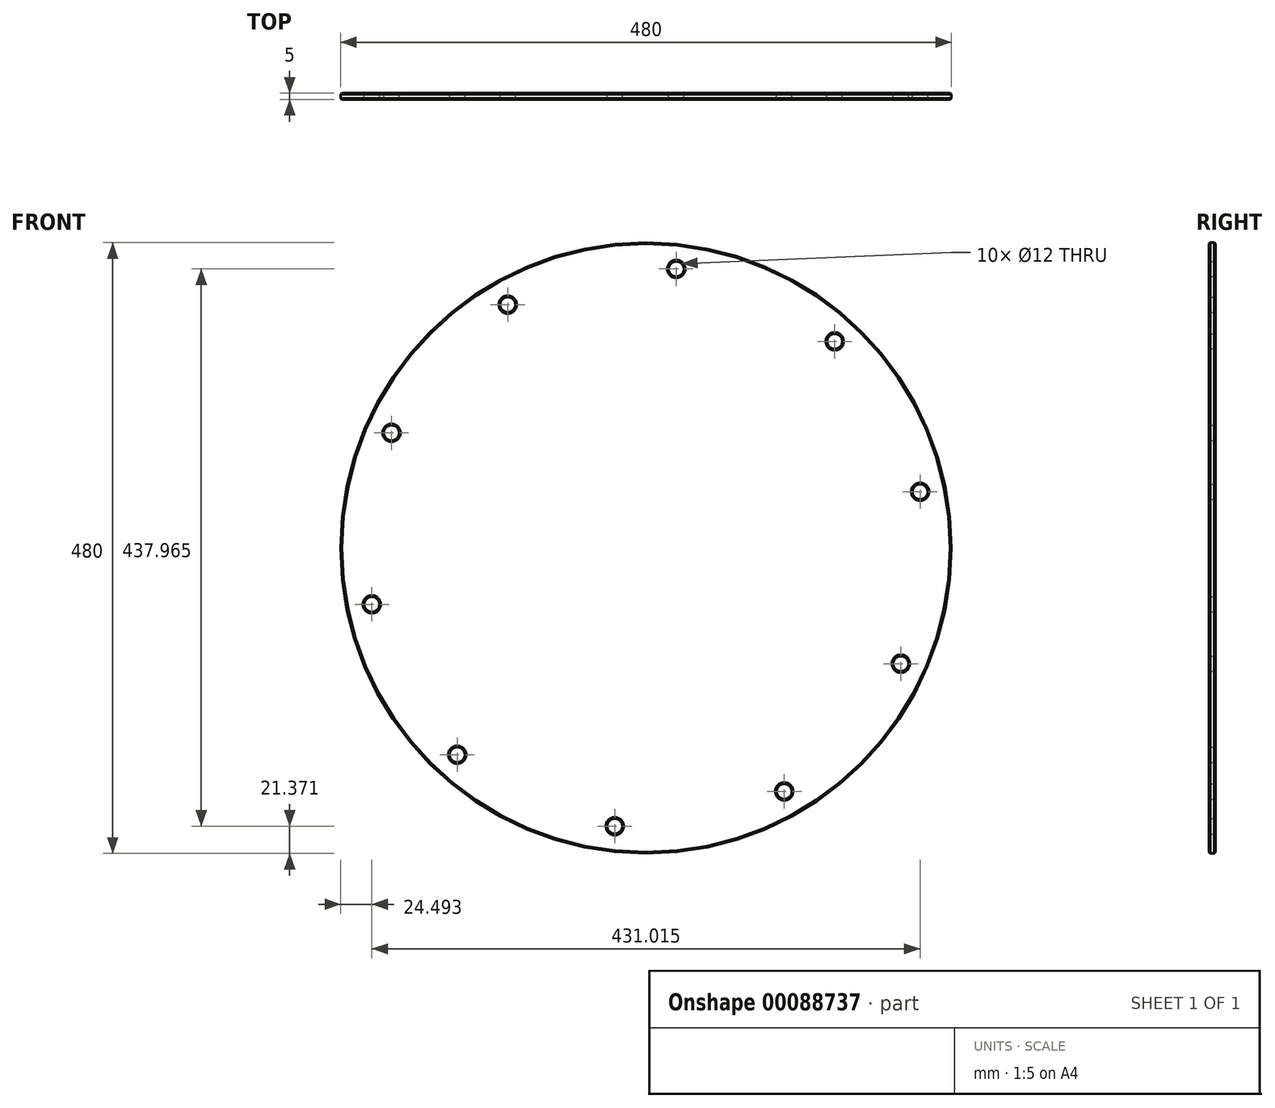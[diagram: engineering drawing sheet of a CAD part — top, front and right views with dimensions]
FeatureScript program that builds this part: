
annotation { "Feature Type Name" : "Feature", "Feature Type Description" : "" }
export const myFeature = defineFeature(function(context is Context, id is Id, definition is map)
    precondition{}
    {
        {
            var Q0;
            Q0=qCreatedBy(makeId("Front.planeOp"),FACE);
            var sketch = newSketch(context, id + "F0", { "sketchPlane" : qUnion([Q0])});
            skCircle(sketch, "E0", {"center": v(0, 0) * mm, "radius": 240 * mm});
            skCircle(sketch, "E1", {"center": v(200.35, -90.89) * mm, "radius": 6 * mm});
            skCircle(sketch, "E2", {"center": v(215.5, 44.23) * mm, "radius": 6 * mm});
            skCircle(sketch, "E3", {"center": v(148.35, 162.46) * mm, "radius": 6 * mm});
            skCircle(sketch, "E4", {"center": v(108.66, -191.3) * mm, "radius": 6 * mm});
            skCircle(sketch, "E5", {"center": v(-24.53, -218.63) * mm, "radius": 6 * mm});
            skCircle(sketch, "E6", {"center": v(-148.35, -162.46) * mm, "radius": 6 * mm});
            skCircle(sketch, "E7", {"center": v(-215.5, -44.23) * mm, "radius": 6 * mm});
            skCircle(sketch, "E8", {"center": v(-200.03, 90.54) * mm, "radius": 6 * mm});
            skCircle(sketch, "E9", {"center": v(-108.66, 191.3) * mm, "radius": 6 * mm});
            skCircle(sketch, "E10", {"center": v(23.82, 219.34) * mm, "radius": 6 * mm});
            skSolve(sketch);
        }
        {
            var Q0;
            Q0=makeQuery(id+"F0.imprint","IMPRINT",FACE,{"disambiguationData":[TD([[makeQuery(id+"F0.imprint","IMPRINT",EDGE,{"derivedFrom":sQuery(id+"F0.wireOp",EDGE,"E0")}),1.0]])]});
            extrude(context, id + "F1", {"entities" : qUnion([Q0]), "depth" : 5 * mm});
        }
        {
            var Q0;
            Q0=makeQuery(id+"F1.opExtrude","CAP_FACE",FACE,{"disambiguationData":[OSD([sQuery(id+"F0.wireOp",EDGE,"E0"),sQuery(id+"F0.wireOp",EDGE,"E1"),sQuery(id+"F0.wireOp",EDGE,"E2"),sQuery(id+"F0.wireOp",EDGE,"E3"),sQuery(id+"F0.wireOp",EDGE,"E4"),sQuery(id+"F0.wireOp",EDGE,"E5"),sQuery(id+"F0.wireOp",EDGE,"E6"),sQuery(id+"F0.wireOp",EDGE,"E7"),sQuery(id+"F0.wireOp",EDGE,"E8"),sQuery(id+"F0.wireOp",EDGE,"E9"),sQuery(id+"F0.wireOp",EDGE,"E10")])],"isStart":false});
            chamfer(context, id + "F2", {"entities" : qUnion([Q0]), "width" : 1 * mm, "tangentPropagation" : true});
        }
        {
            var Q0;
            Q0=makeQuery(id+"F1.opExtrude","CAP_FACE",FACE,{"disambiguationData":[OSD([sQuery(id+"F0.wireOp",EDGE,"E0"),sQuery(id+"F0.wireOp",EDGE,"E1"),sQuery(id+"F0.wireOp",EDGE,"E2"),sQuery(id+"F0.wireOp",EDGE,"E3"),sQuery(id+"F0.wireOp",EDGE,"E4"),sQuery(id+"F0.wireOp",EDGE,"E5"),sQuery(id+"F0.wireOp",EDGE,"E6"),sQuery(id+"F0.wireOp",EDGE,"E7"),sQuery(id+"F0.wireOp",EDGE,"E8"),sQuery(id+"F0.wireOp",EDGE,"E9"),sQuery(id+"F0.wireOp",EDGE,"E10")])],"isStart":true});
            chamfer(context, id + "F3", {"entities" : qUnion([Q0]), "width" : 1 * mm, "tangentPropagation" : true});
        }
    });
